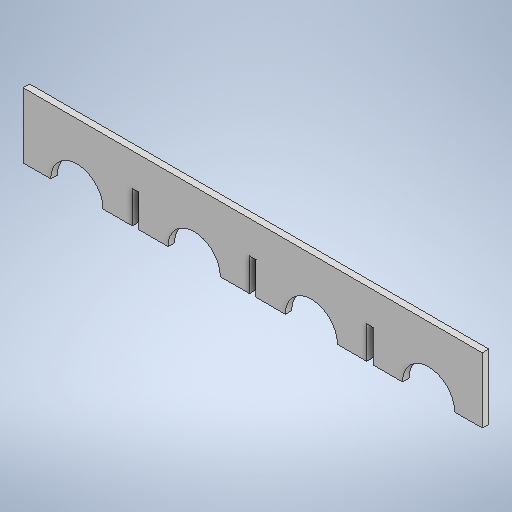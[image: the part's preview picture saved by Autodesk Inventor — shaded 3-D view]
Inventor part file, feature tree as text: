
AUTODESK INVENTOR PART (.ipt)
format: ipt  version: 2025 (Build 290162010, 162A)  size: 297,984 bytes
history: native  units: mm
features: extrude x2, sketch x2
ambient origin geometry x8: Origin, YZ Plane, XZ Plane, XY Plane, X Axis, Y Axis, Z Axis, Center Point
bodies: Solid1 (feature_tree)
feature tree (4):
  extrude  "Extrusion1"  Depth=100.0mm TaperAngle=0.0deg
  extrude  "Extrusion3"  Depth=180.0mm
  sketch  "Sketch1"  dims[d0=800.0mm d3=100.0mm d4=0.0mm]
  sketch  "Sketch3"  dims[d32=10.0mm d33=180.0mm d34=705.0mm d35=80.0mm d36=90.0mm d37=80.0mm d38=180.0mm d39=80.0mm d40=80.0mm d41=90.0mm d42=180.0mm d51=0.0mm d52=0.0mm d53=10.0mm d54=180.0mm d55=50.0mm d56=10.0mm d57=50.0mm d58=10.0mm d59=50.0mm d60=180.0mm]
